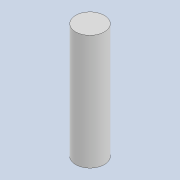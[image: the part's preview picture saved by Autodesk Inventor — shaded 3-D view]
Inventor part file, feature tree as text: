
AUTODESK INVENTOR PART (.ipt)
format: ipt  version: 2020 (Build 240168000, 168)  size: 72,192 bytes
history: native  units: mm
features: extrude x1, sketch x1
ambient origin geometry x8: Origin, YZ Plane, XZ Plane, XY Plane, X Axis, Y Axis, Z Axis, Center Point
bodies: Solid1 (feature_tree)
feature tree (2):
  extrude  "Extrusion1"  Depth=8.0mm TaperAngle=0.0deg
  sketch  "Sketch1"  dims[d0=2.0mm d1=8.0mm d2=0.0mm]
